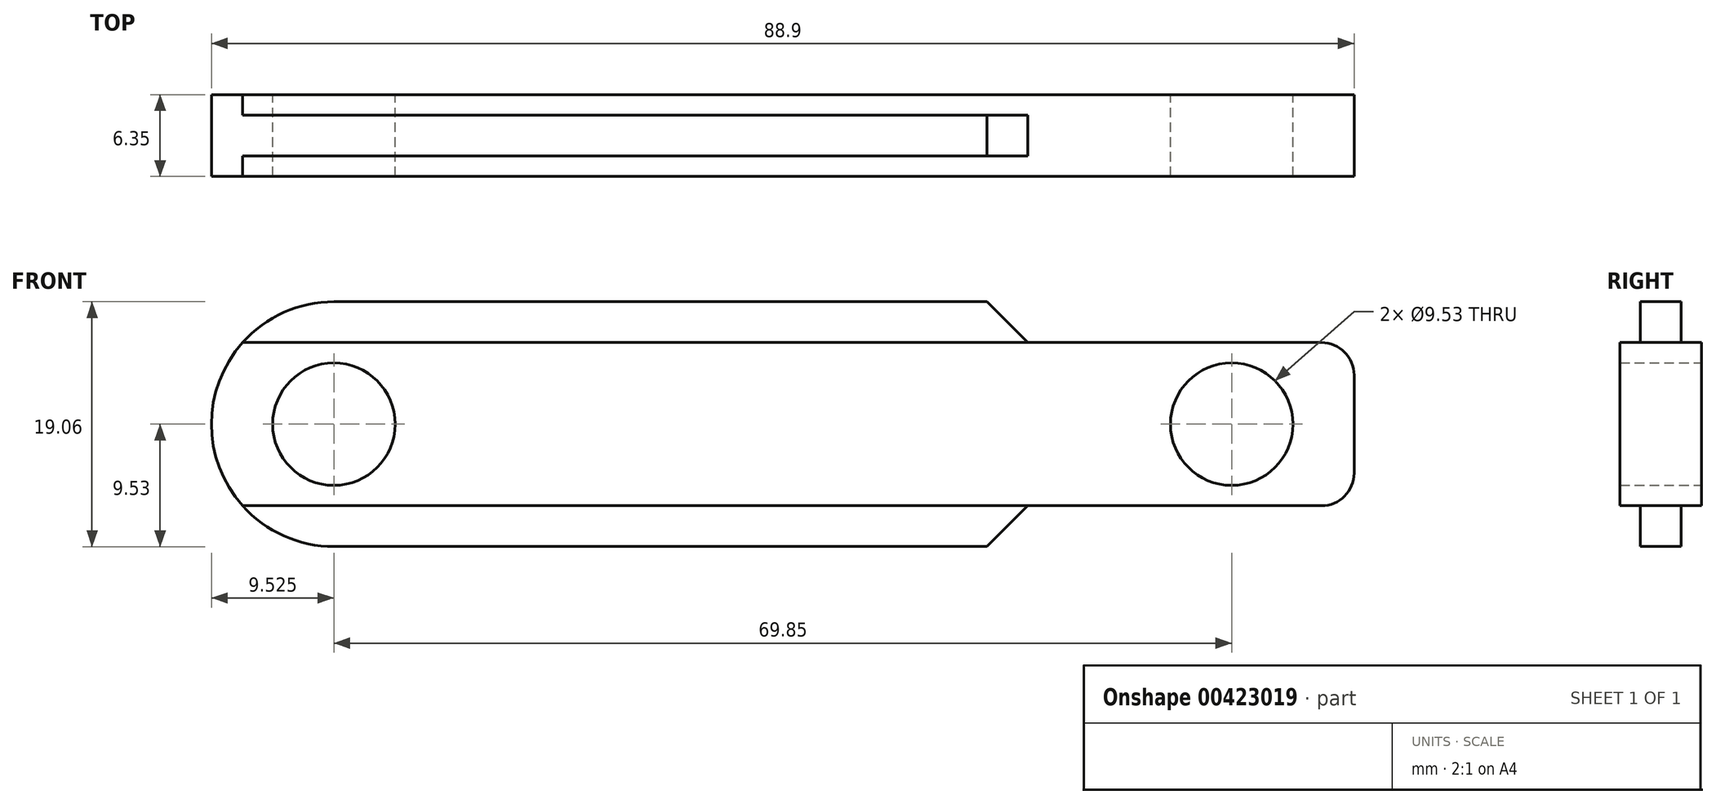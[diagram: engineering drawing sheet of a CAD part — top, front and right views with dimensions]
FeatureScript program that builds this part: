
annotation { "Feature Type Name" : "Feature", "Feature Type Description" : "" }
export const myFeature = defineFeature(function(context is Context, id is Id, definition is map)
    precondition{}
    {
        {
            var Q0;
            Q0=qCreatedBy(makeId("Front.planeOp"),FACE);
            var sketch = newSketch(context, id + "F0", { "sketchPlane" : qUnion([Q0])});
            skLineSegment(sketch, "E0.bottom", {"start": v(41.91, 6.35) * mm, "end": v(-41.91, 6.35) * mm});
            skLineSegment(sketch, "E0.top", {"start": v(41.91, -6.35) * mm, "end": v(-41.91, -6.35) * mm});
            skLineSegment(sketch, "E0.left", {"start": v(44.45, 3.81) * mm, "end": v(44.45, -3.81) * mm});
            skLineSegment(sketch, "E0.right", {"start": v(-44.45, 3.81) * mm, "end": v(-44.45, -3.81) * mm});
            skPoint(sketch, "E0.middle", {"position": v(0, 0) * mm});
            skCircle(sketch, "E1", {"center": v(-34.93, 0) * mm, "radius": 4.76 * mm});
            skCircle(sketch, "E2", {"center": v(34.93, 0) * mm, "radius": 4.76 * mm});
            skPoint(sketch, "E3.visualSharp", {"position": v(-44.45, 6.35) * mm});
            skArc(sketch, "E3.filletArc", {"start": v(-41.91, 6.35) * mm, "mid": v(-43.7, 5.6) * mm, "end": v(-44.45, 3.8) * mm});
            skPoint(sketch, "E4.visualSharp", {"position": v(-44.45, -6.35) * mm});
            skArc(sketch, "E4.filletArc", {"start": v(-44.45, -3.8) * mm, "mid": v(-43.7, -5.6) * mm, "end": v(-41.91, -6.35) * mm});
            skPoint(sketch, "E5.visualSharp", {"position": v(44.45, 6.35) * mm});
            skArc(sketch, "E5.filletArc", {"start": v(44.45, 3.81) * mm, "mid": v(43.7, 5.6) * mm, "end": v(41.91, 6.35) * mm});
            skPoint(sketch, "E6.visualSharp", {"position": v(44.45, -6.35) * mm});
            skArc(sketch, "E6.filletArc", {"start": v(41.91, -6.35) * mm, "mid": v(43.7, -5.6) * mm, "end": v(44.45, -3.81) * mm});
            skSolve(sketch);
        }
        {
            var Q0;
            Q0=qSketchRegion(id+"F0",true);
            extrude(context, id + "F1", {"entities" : qUnion([Q0]), "depth" : 6.35 * mm});
        }
        {
            var Q0;
            Q0=qCreatedBy(makeId("Top.planeOp"),FACE);
            var sketch = newSketch(context, id + "F2", { "sketchPlane" : qUnion([Q0])});
            skLineSegment(sketch, "E7", {"start": v(-44.6, -3.18) * mm, "end": v(45.4, -3.18) * mm});
            skSolve(sketch);
        }
        {
            var Q0;
            Q0=sQuery(id+"F2.wireOp",EDGE,"E7");
            var Q1;
            Q1=makeQuery(id+"F1.opExtrude","CAP_FACE",FACE,{"disambiguationData":[OSD([sQuery(id+"F0.wireOp",EDGE,"E0.bottom"),sQuery(id+"F0.wireOp",EDGE,"E0.top"),sQuery(id+"F0.wireOp",EDGE,"E0.left"),sQuery(id+"F0.wireOp",EDGE,"E0.right"),sQuery(id+"F0.wireOp",EDGE,"E1"),sQuery(id+"F0.wireOp",EDGE,"E2"),sQuery(id+"F0.wireOp",EDGE,"E3.filletArc"),sQuery(id+"F0.wireOp",EDGE,"E4.filletArc"),sQuery(id+"F0.wireOp",EDGE,"E5.filletArc"),sQuery(id+"F0.wireOp",EDGE,"E6.filletArc")])],"isStart":false});
            cPlane(context, id + "F3", {"entities" : qUnion([Q0, Q1]), "cplaneType" : CPlaneType.LINE_ANGLE, "offset" : 25.4 * mm, "angle" : 0 * degree, "width" : 152.4 * mm, "height" : 152.4 * mm});
        }
        {
            var Q0;
            Q0=qCreatedBy(id+"F3.planeOp",FACE);
            var sketch = newSketch(context, id + "F4", { "sketchPlane" : qUnion([Q0])});
            skLineSegment(sketch, "E8.bottom", {"start": v(-19.05, -9.53) * mm, "end": v(44.45, -9.53) * mm});
            skLineSegment(sketch, "E8.top", {"start": v(-19.05, 9.52) * mm, "end": v(44.45, 9.53) * mm});
            skLineSegment(sketch, "E8.left", {"start": v(-19.05, -9.52) * mm, "end": v(-19.05, 9.52) * mm});
            skLineSegment(sketch, "E8.right", {"start": v(44.45, -9.53) * mm, "end": v(44.45, 9.53) * mm});
            skLineSegment(sketch, "E9", {"start": v(44.45, 0) * mm, "end": v(36.38, 5.46) * mm});
            skLineSegment(sketch, "E10", {"start": v(36.38, 5.46) * mm, "end": v(-19.05, 5.46) * mm});
            skLineSegment(sketch, "E11", {"start": v(44.45, 0) * mm, "end": v(36.38, -5.46) * mm});
            skLineSegment(sketch, "E12", {"start": v(36.38, -5.46) * mm, "end": v(-19.05, -5.46) * mm});
            skLineSegment(sketch, "E13", {"start": v(-19.05, 5.46) * mm, "end": v(-19.05, -5.46) * mm});
            skLineSegment(sketch, "E14", {"start": v(29.73, 5.46) * mm, "end": v(29.73, -5.46) * mm});
            skSolve(sketch);
        }
        {
            var Q0;
            {var subQ1=sQuery(id+"F4.wireOp",EDGE,"E8.top");Q0=makeQuery(id+"F4.imprint","IMPRINT",FACE,{"disambiguationData":[TD([[makeQuery(id+"F4.imprint","IMPRINT",EDGE,{"derivedFrom":subQ1}),-1.0]])]});}
            var Q1;
            {var subQ2=sQuery(id+"F4.wireOp",EDGE,"E8.bottom");Q1=makeQuery(id+"F4.imprint","IMPRINT",FACE,{"disambiguationData":[TD([[makeQuery(id+"F4.imprint","IMPRINT",EDGE,{"derivedFrom":subQ2}),1.0]])]});}
            extrude(context, id + "F5", {"entities" : qUnion([Q0, Q1]), "operationType" : NewBodyOperationType.ADD, "depth" : 1.59 * mm, "hasSecondDirection" : true, "secondDirectionOppositeDirection" : true, "secondDirectionDepth" : 1.59 * mm});
        }
        {
            var Q0;
            Q0=makeQuery(id+"F5.opExtrude","SWEPT_EDGE",EDGE,{"disambiguationData":[OSD([sQuery(id+"F4.wireOp",EDGE,"E8.top"),sQuery(id+"F4.wireOp",EDGE,"E8.left")])]});
            var Q1;
            Q1=makeQuery(id+"F5.opExtrude","SWEPT_EDGE",EDGE,{"disambiguationData":[OSD([sQuery(id+"F4.wireOp",EDGE,"E8.bottom"),sQuery(id+"F4.wireOp",EDGE,"E8.left")])]});
            chamfer(context, id + "F6", {"entities" : qUnion([Q0, Q1]), "width" : 3.17 * mm, "tangentPropagation" : true});
        }
        {
            var Q0;
            Q0=makeQuery(id+"F5.opExtrude","SWEPT_EDGE",EDGE,{"disambiguationData":[OSD([sQuery(id+"F4.wireOp",EDGE,"E8.top"),sQuery(id+"F4.wireOp",EDGE,"E8.right")])]});
            var Q1;
            Q1=makeQuery(id+"F5.opExtrude","SWEPT_EDGE",EDGE,{"disambiguationData":[OSD([sQuery(id+"F4.wireOp",EDGE,"E8.bottom"),sQuery(id+"F4.wireOp",EDGE,"E8.right")])]});
            fillet(context, id + "F7", {"entities" : qUnion([Q0, Q1]), "radius" : 9.52 * mm, "tangentPropagation" : true, "allowEdgeOverflow" : false});
        }
    });
